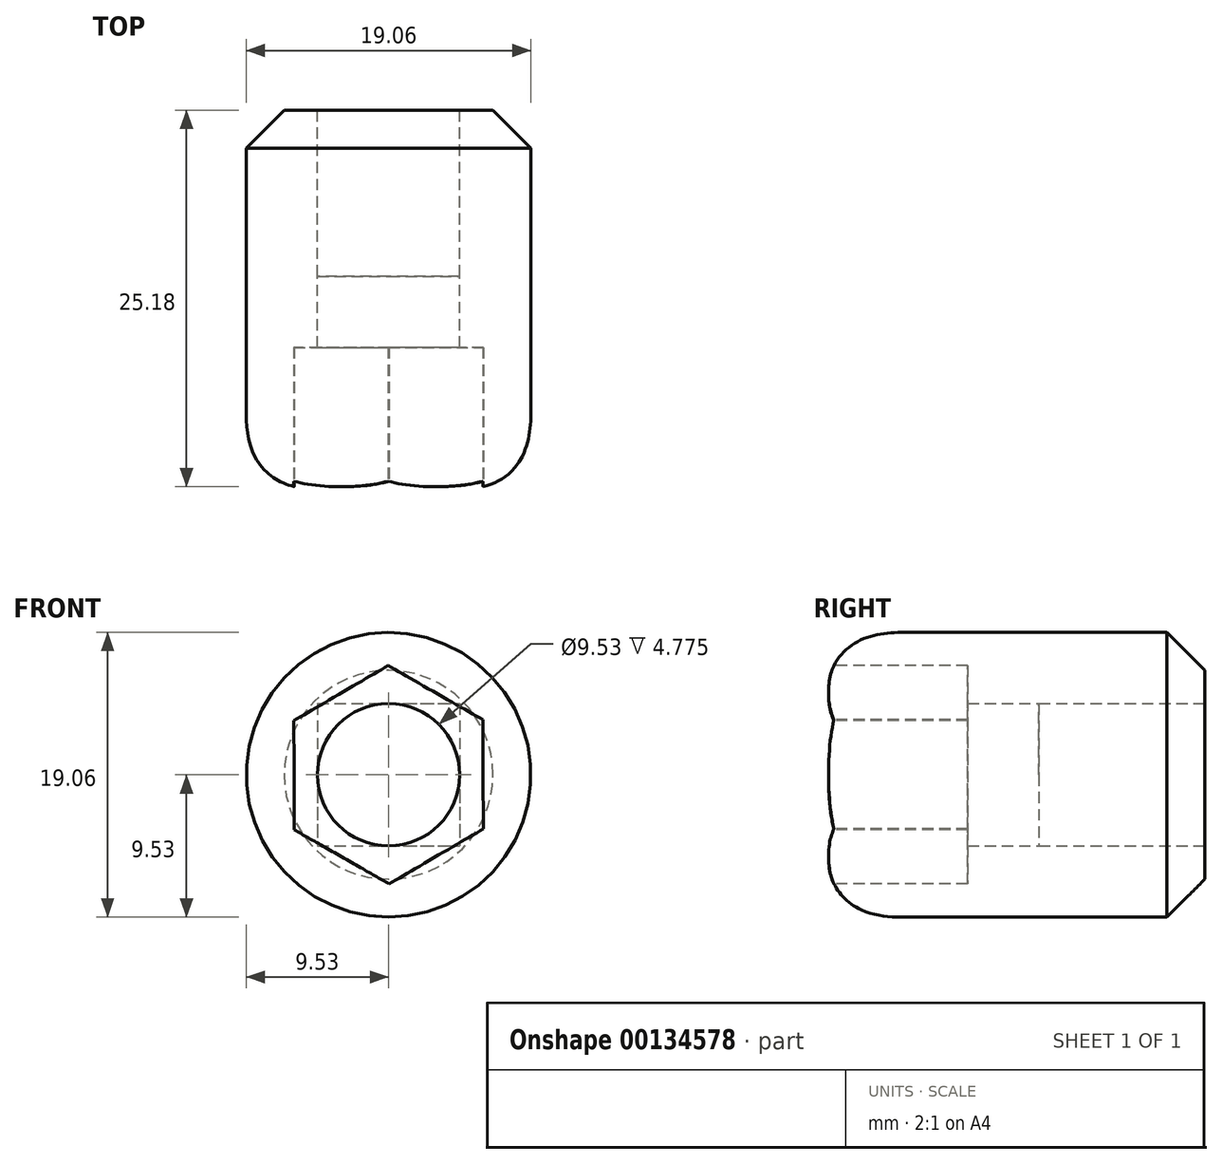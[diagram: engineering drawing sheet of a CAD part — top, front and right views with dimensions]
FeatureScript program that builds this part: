
annotation { "Feature Type Name" : "Feature", "Feature Type Description" : "" }
export const myFeature = defineFeature(function(context is Context, id is Id, definition is map)
    precondition{}
    {
        {
            var Q0;
            Q0=qCreatedBy(makeId("Front.planeOp"),FACE);
            var sketch = newSketch(context, id + "F0", { "sketchPlane" : qUnion([Q0])});
            skCircle(sketch, "E0", {"center": v(0, 0) * mm, "radius": 9.53 * mm});
            skSolve(sketch);
        }
        {
            var Q0;
            Q0 = qSketchRegion(id + "F0", true);
            extrude(context, id + "F1", {"entities" : qUnion([Q0]), "depth" : 25.4 * mm});
        }
        {
            var Q0;
            Q0=qCreatedBy(makeId("Front.planeOp"),FACE);
            var sketch = newSketch(context, id + "F2", { "sketchPlane" : qUnion([Q0])});
            skLineSegment(sketch, "E1.bottom", {"start": v(-4.76, 4.76) * mm, "end": v(4.76, 4.76) * mm});
            skLineSegment(sketch, "E1.top", {"start": v(-4.76, -4.76) * mm, "end": v(4.76, -4.76) * mm});
            skLineSegment(sketch, "E1.left", {"start": v(-4.76, 4.76) * mm, "end": v(-4.76, -4.76) * mm});
            skLineSegment(sketch, "E1.right", {"start": v(4.76, 4.76) * mm, "end": v(4.76, -4.76) * mm});
            skPoint(sketch, "E1.middle", {"position": v(0, 0) * mm});
            skCircle(sketch, "E2", {"center": v(0, 0) * mm, "radius": 4.76 * mm});
            skSolve(sketch);
        }
        {
            var Q0;
            Q0=makeQuery(id+"F1.opExtrude","CAP_FACE",FACE,{"disambiguationData":[OSD([sQuery(id+"F0.wireOp",EDGE,"E0")])],"isStart":false});
            var Q1;
            {var subQ0=sQuery(id+"F2.wireOp",EDGE,"E2");var subQ1=makeQuery(id+"F2.imprint","INTERSECT",VERTEX,{"derivedFrom":[sQuery(id+"F2.wireOp",EDGE,"E1.bottom"),subQ0]});Q1=makeQuery(id+"F2.imprint","IMPRINT",FACE,{"disambiguationData":[TD([[makeQuery(id+"F2.imprint","IMPRINT",EDGE,{"disambiguationData":[TD([[subQ1,1.0]])],"derivedFrom":subQ0}),1.0]])]});}
            extrude(context, id + "F3", {"entities" : qUnion([Q0, Q1]), "operationType" : NewBodyOperationType.REMOVE, "endBound" : BoundingType.THROUGH_ALL, "depth" : 25.4 * mm});
        }
        {
            var Q0;
            Q0 = qSketchRegion(id + "F2", true);
            extrude(context, id + "F4", {"entities" : qUnion([Q0]), "operationType" : NewBodyOperationType.REMOVE, "depth" : 11.1 * mm});
        }
        {
            var Q0;
            Q0=makeQuery(id+"F1.opExtrude","CAP_FACE",FACE,{"disambiguationData":[OSD([sQuery(id+"F0.wireOp",EDGE,"E0")])],"isStart":false});
            var sketch = newSketch(context, id + "F5", { "sketchPlane" : qUnion([Q0])});
            skCircle(sketch, "E3.cCircle", {"center": v(0, 0) * mm, "radius": 6.32 * mm, "construction": true});
            skLineSegment(sketch, "E3.0", {"start": v(-6.34, 3.62) * mm, "end": v(-0.04, 7.3) * mm});
            skLineSegment(sketch, "E3.1", {"start": v(-0.04, 7.3) * mm, "end": v(6.3, 3.68) * mm});
            skLineSegment(sketch, "E3.2", {"start": v(6.3, 3.68) * mm, "end": v(6.34, -3.62) * mm});
            skLineSegment(sketch, "E3.3", {"start": v(6.34, -3.62) * mm, "end": v(0.04, -7.3) * mm});
            skLineSegment(sketch, "E3.4", {"start": v(0.04, -7.3) * mm, "end": v(-6.3, -3.68) * mm});
            skLineSegment(sketch, "E3.5", {"start": v(-6.3, -3.68) * mm, "end": v(-6.34, 3.62) * mm});
            skPoint(sketch, "E3.0.midPoint", {"position": v(-3.2, 5.46) * mm});
            skSolve(sketch);
        }
        {
            var Q0;
            Q0=makeQuery(id+"F5.imprint","IMPRINT",FACE,{"disambiguationData":[TD([[makeQuery(id+"F5.imprint","IMPRINT",EDGE,{"derivedFrom":sQuery(id+"F5.wireOp",EDGE,"E3.0")}),-1.0]])]});
            extrude(context, id + "F6", {"entities" : qUnion([Q0]), "operationType" : NewBodyOperationType.REMOVE, "oppositeDirection" : true, "depth" : 9.52 * mm});
        }
        {
            var Q0;
            Q0=makeQuery(id+"F1.opExtrude","CAP_EDGE",EDGE,{"disambiguationData":[OSD([sQuery(id+"F0.wireOp",EDGE,"E0")])],"isStart":false});
            fillet(context, id + "F7", {"entities" : qUnion([Q0]), "radius" : 5.08 * mm, "tangentPropagation" : true, "rho" : 0.5, "crossSection" : FilletCrossSection.CONIC, "allowEdgeOverflow" : false});
        }
        {
            var Q0;
            Q0=makeQuery(id+"F1.opExtrude","CAP_EDGE",EDGE,{"disambiguationData":[OSD([sQuery(id+"F0.wireOp",EDGE,"E0")])],"isStart":true});
            chamfer(context, id + "F8", {"entities" : qUnion([Q0]), "width" : 2.54 * mm, "tangentPropagation" : true});
        }
    });
